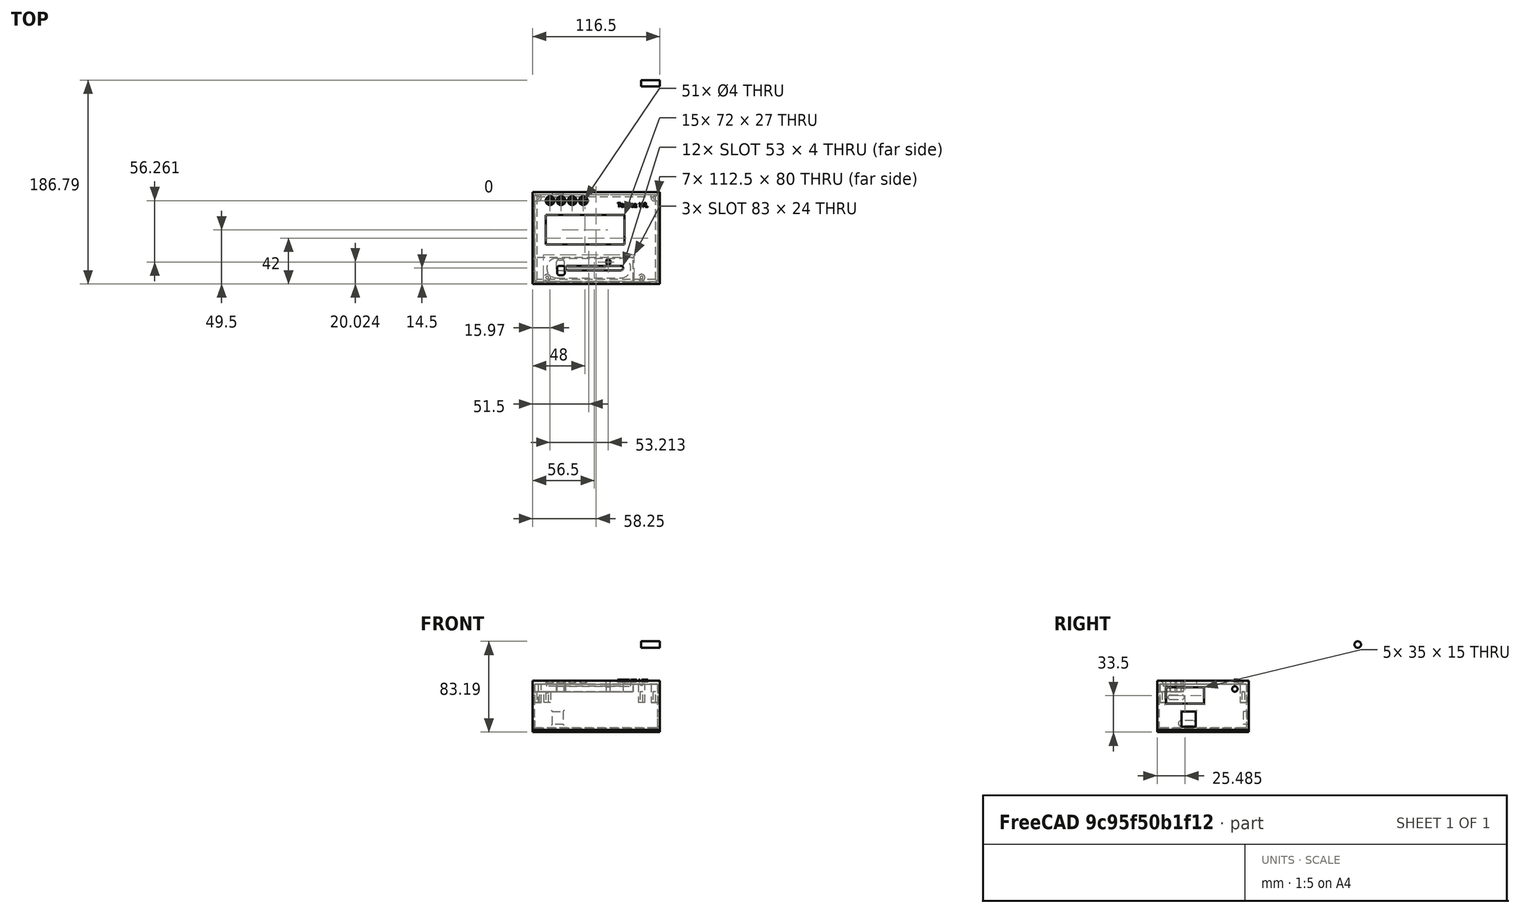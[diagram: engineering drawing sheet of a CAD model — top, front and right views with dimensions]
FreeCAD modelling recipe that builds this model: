
FCSTD DOCUMENT  (FreeCAD 0.17R7682 (Git))
Label: Modelodelgabinete4
License: CC-BY 3.0
LicenseURL: http://creativecommons.org/licenses/by/3.0/
objects: Sketcher::SketchObject×23, PartDesign::Pocket×14, PartDesign::Fillet×14, Part::Fillet×10, PartDesign::Pad×9, Part::Cut×6, Part::Extrusion×6, Drawing::FeatureViewPart×3, PartDesign::Chamfer×2, Part::Part2DObjectPython×1, Drawing::FeaturePage×1
note: 108 computed .brp shape members not serialized (recipe doc carries the construction recipe); baked Part::Feature solids carry a one-line shape summary decoded from their .brp

FEATURE [Sketcher::SketchObject] Sketch
  MapMode = 5
  sketch-geometry (5):
    g0: LineSegment StartX=0 StartY=0 StartZ=0 EndX=116.5 EndY=0 EndZ=0
    g1: LineSegment StartX=116.5 StartY=0 StartZ=0 EndX=116.5 EndY=-84 EndZ=0
    g2: LineSegment StartX=116.5 StartY=-84 StartZ=0 EndX=0 EndY=-84 EndZ=0
    g3: LineSegment StartX=0 StartY=-84 StartZ=0 EndX=0 EndY=0 EndZ=0
    g4: GeomPoint [constr] X=0 Y=0 Z=0
  constraints (12):
    c: Coincident(g0,g1)
    c: Coincident(g1,g2)
    c: Coincident(g2,g3)
    c: Coincident(g3,g0)
    c: Horizontal(g0)
    c: Horizontal(g2)
    c: Vertical(g1)
    c: Vertical(g3)
    c: Coincident(g4,g-1)
    c: Coincident(g0,g-1)
    c: DistanceX(g0) = 116.5
    c: DistanceY(g3) = 84
FEATURE [PartDesign::Pad] Pad
  Length = 45
  Length2 = 100
  Type = 0
FEATURE [Sketcher::SketchObject] Sketch001
  MapMode = 5
  Placement = pos=(0,0,0) rot=(1,0,0;1.5708rad)
  sketch-geometry (4):
    g0: LineSegment StartX=18 StartY=5 StartZ=0 EndX=28 EndY=5 EndZ=0
    g1: LineSegment StartX=28 StartY=5 StartZ=0 EndX=28 EndY=17 EndZ=0
    g2: LineSegment StartX=28 StartY=17 StartZ=0 EndX=18 EndY=17 EndZ=0
    g3: LineSegment StartX=18 StartY=17 StartZ=0 EndX=18 EndY=5 EndZ=0
  constraints (12):
    c: Coincident(g0,g1)
    c: Coincident(g1,g2)
    c: Coincident(g2,g3)
    c: Coincident(g3,g0)
    c: Horizontal(g0)
    c: Horizontal(g2)
    c: Vertical(g1)
    c: Vertical(g3)
    c: DistanceX(g-1,g0) = 18
    c: DistanceY(g-1,g0) = 5
    c: DistanceX(g0) = 10
    c: DistanceY(g1) = 12
FEATURE [PartDesign::Pad] Pad001
  Length = 5
  Length2 = 100
  Placement = pos=(0,0,0) rot=(1,0,0;1.5708rad)
  Type = 0
FEATURE [Part::Cut] Cut
  Base = -> Pad
  Tool = -> Pad001
FEATURE [Sketcher::SketchObject] Sketch002
  MapMode = 5
  Placement = pos=(0,0,45) rot=(0,0,1;0rad)
  sketch-geometry (4):
    g0: LineSegment StartX=11.5 StartY=-20.5 StartZ=0 EndX=84.5 EndY=-20.5 EndZ=0
    g1: LineSegment StartX=84.5 StartY=-20.5 StartZ=0 EndX=84.5 EndY=-48.5 EndZ=0
    g2: LineSegment StartX=84.5 StartY=-48.5 StartZ=0 EndX=11.5 EndY=-48.5 EndZ=0
    g3: LineSegment StartX=11.5 StartY=-48.5 StartZ=0 EndX=11.5 EndY=-20.5 EndZ=0
  constraints (12):
    c: Coincident(g0,g1)
    c: Coincident(g1,g2)
    c: Coincident(g2,g3)
    c: Coincident(g3,g0)
    c: Horizontal(g0)
    c: Horizontal(g2)
    c: Vertical(g1)
    c: Vertical(g3)
    c: DistanceY(g-1,g0) = -20.5
    c: DistanceX(g-1,g0) = 11.5
    c: DistanceY(g3) = 28
    c: DistanceX(g2) = -73
FEATURE [PartDesign::Pocket] Pocket
  Length = 5
  Type = 0
FEATURE [Sketcher::SketchObject] Sketch003
  MapMode = 5
  sketch-geometry (4):
    g0: LineSegment StartX=2 StartY=-2 StartZ=0 EndX=114.5 EndY=-2 EndZ=0
    g1: LineSegment StartX=114.5 StartY=-2 StartZ=0 EndX=114.5 EndY=-82 EndZ=0
    g2: LineSegment StartX=114.5 StartY=-82 StartZ=0 EndX=2 EndY=-82 EndZ=0
    g3: LineSegment StartX=2 StartY=-82 StartZ=0 EndX=2 EndY=-2 EndZ=0
  constraints (12):
    c: Coincident(g0,g1)
    c: Coincident(g1,g2)
    c: Coincident(g2,g3)
    c: Coincident(g3,g0)
    c: Horizontal(g0)
    c: Horizontal(g2)
    c: Vertical(g1)
    c: Vertical(g3)
    c: DistanceY(g-1,g0) = -2
    c: DistanceX(g-1,g0) = 2
    c: DistanceX(g2) = -112.5
    c: DistanceY(g1) = -80
FEATURE [PartDesign::Pad] Pad002
  Length = 42
  Length2 = 100
  Type = 0
FEATURE [Part::Cut] Cut001
  Base = -> Pocket
  Tool = -> Pad002
FEATURE [Sketcher::SketchObject] Sketch004
  ExternalGeometry = -> [Cut001]
  MapMode = 5
  Placement = pos=(0,0,0) rot=(0.57735,-0.57735,-0.57735;2.0944rad)
  sketch-geometry (4):
    g0: ArcOfCircle CenterX=72 CenterY=30 CenterZ=0 NormalX=0 NormalY=0 NormalZ=1 Radius=2 StartAngle=4.7124 EndAngle=7.85397
    g1: ArcOfCircle CenterX=61 CenterY=30 CenterZ=0 NormalX=0 NormalY=0 NormalZ=1 Radius=2 StartAngle=1.57079 EndAngle=4.71239
    g2: LineSegment StartX=72 StartY=32 StartZ=0 EndX=61 EndY=32 EndZ=0
    g3: LineSegment StartX=72 StartY=28 StartZ=0 EndX=61 EndY=28 EndZ=0
  constraints (14):
    c: Tangent(g0,g2)
    c: Tangent(g0,g3)
    c: Tangent(g1,g2)
    c: Tangent(g1,g3)
    c: Coincident(g0,g3)
    c: Coincident(g0,g2)
    c: Coincident(g2,g1)
    c: Coincident(g3,g1)
    c: Horizontal(g2)
    c: Equal(g0,g1)
    c: DistanceX(g0,g-3) = 12
    c: DistanceX(g1,g0) = 11
    c: Radius(g0) = 2
    c: DistanceY(g-3,g0) = 30
FEATURE [PartDesign::Pocket] Pocket001
  Length = 5
  Type = 0
FEATURE [Sketcher::SketchObject] Sketch005
  MapMode = 5
  Placement = pos=(0,0,0) rot=(0.57735,-0.57735,-0.57735;2.0944rad)
  sketch-geometry (4):
    g0: ArcOfCircle CenterX=51 CenterY=6 CenterZ=0 NormalX=0 NormalY=0 NormalZ=1 Radius=2.5 StartAngle=1.57079 EndAngle=4.71239
    g1: ArcOfCircle CenterX=62 CenterY=6 CenterZ=0 NormalX=0 NormalY=0 NormalZ=1 Radius=2.5 StartAngle=4.7124 EndAngle=7.85397
    g2: LineSegment StartX=51 StartY=3.5 StartZ=0 EndX=62 EndY=3.5 EndZ=0
    g3: LineSegment StartX=51 StartY=8.5 StartZ=0 EndX=62 EndY=8.5 EndZ=0
  constraints (13):
    c: Tangent(g0,g2)
    c: Tangent(g0,g3)
    c: Tangent(g1,g2)
    c: Tangent(g1,g3)
    c: Coincident(g0,g3)
    c: Coincident(g0,g2)
    c: Coincident(g2,g1)
    c: Coincident(g3,g1)
    c: Horizontal(g2)
    c: Equal(g0,g1)
    c: DistanceY(g-1,g0) = 6
    c: Radius(g0) = 2.5
    c: DistanceX(g0,g1) = 11
FEATURE [PartDesign::Pocket] Pocket002
  Length = 5
  Type = 0
FEATURE [Sketcher::SketchObject] Sketch006
  ExternalGeometry = -> [Pocket002]
  MapMode = 5
  Placement = pos=(0,0,45) rot=(0,0,1;0rad)
  sketch-geometry (4):
    g0: ArcOfCircle CenterX=32 CenterY=-69.5 CenterZ=0 NormalX=0 NormalY=0 NormalZ=1 Radius=2 StartAngle=1.5708 EndAngle=4.71239
    g1: ArcOfCircle CenterX=81 CenterY=-69.5 CenterZ=0 NormalX=0 NormalY=0 NormalZ=1 Radius=2 StartAngle=4.71239 EndAngle=7.85398
    g2: LineSegment StartX=32 StartY=-71.5 StartZ=0 EndX=81 EndY=-71.5 EndZ=0
    g3: LineSegment StartX=32 StartY=-67.5 StartZ=0 EndX=81 EndY=-67.5 EndZ=0
  constraints (14):
    c: Tangent(g0,g2)
    c: Tangent(g0,g3)
    c: Tangent(g1,g2)
    c: Tangent(g1,g3)
    c: Coincident(g0,g3)
    c: Coincident(g0,g2)
    c: Coincident(g2,g1)
    c: Coincident(g3,g1)
    c: Horizontal(g2)
    c: Equal(g0,g1)
    c: DistanceY(g-3,g0) = 14.5
    c: Radius(g1) = 2
    c: DistanceX(g0,g-3) = -32
    c: DistanceX(g0,g1) = 49
FEATURE [PartDesign::Pocket] Pocket003
  Length = 5
  Type = 0
FEATURE [PartDesign::Pocket] Pocket004
  Length = 5
  Type = 0
FEATURE [Sketcher::SketchObject] Sketch008
  MapMode = 5
  Placement = pos=(0,0,45) rot=(0,0,1;0rad)
  sketch-geometry (5):
    g0: Circle CenterX=15.97 CenterY=-7.715 CenterZ=0 NormalX=0 NormalY=0 NormalZ=1 Radius=2
    g1: Circle CenterX=26.13 CenterY=-7.715 CenterZ=0 NormalX=0 NormalY=0 NormalZ=1 Radius=2
    g2: Circle CenterX=36.29 CenterY=-7.715 CenterZ=0 NormalX=0 NormalY=0 NormalZ=1 Radius=2
    g3: Circle CenterX=46.45 CenterY=-7.715 CenterZ=0 NormalX=0 NormalY=0 NormalZ=1 Radius=2
    g4: Circle CenterX=69.183 CenterY=-63.976 CenterZ=0 NormalX=0 NormalY=0 NormalZ=1 Radius=2
  constraints (15):
    c: DistanceX(g-1,g0) = 15.97
    c: Radius(g0) = 2
    c: Equal(g1,g0)
    c: DistanceY(g1,g0) = 0
    c: DistanceX(g1,g0) = -10.16
    c: Equal(g1,g2)
    c: DistanceX(g2,g1) = -10.16
    c: DistanceY(g1,g2) = 0
    c: Equal(g3,g2)
    c: DistanceY(g2,g3) = 0
    c: DistanceX(g2,g3) = 10.16
    c: DistanceY(g-1,g0) = -7.715
    c: DistanceX(g-1,g4) = 69.183
    c: Radius(g4) = 2
    c: DistanceY(g-1,g4) = -63.976
FEATURE [PartDesign::Pocket] Pocket005
  Length = 10
  Type = 2
FEATURE [Sketcher::SketchObject] Sketch009
  MapMode = 5
  Placement = pos=(116.5,0,0) rot=(0.57735,0.57735,0.57735;2.0944rad)
  sketch-geometry (12):
    g0: LineSegment StartX=-76.015 StartY=39 StartZ=0 EndX=-41.015 EndY=39 EndZ=0
    g1: LineSegment StartX=-41.015 StartY=39 StartZ=0 EndX=-41.015 EndY=24 EndZ=0
    g2: LineSegment StartX=-41.015 StartY=24 StartZ=0 EndX=-76.015 EndY=24 EndZ=0
    g3: LineSegment StartX=-76.015 StartY=24 StartZ=0 EndX=-76.015 EndY=39 EndZ=0
    g4: LineSegment [constr] StartX=-58.515 StartY=5.11299 StartZ=0 EndX=-58.515 EndY=39.8089 EndZ=0
    g5: LineSegment [constr] StartX=-79.1576 StartY=31.5 StartZ=0 EndX=-35.4167 EndY=31.5 EndZ=0
    g6: LineSegment [constr] StartX=-61.5 StartY=10 StartZ=0 EndX=-48.5 EndY=10 EndZ=0
    g7: LineSegment StartX=-61.5 StartY=17 StartZ=0 EndX=-48.5 EndY=17 EndZ=0
    g8: LineSegment StartX=-48.5 StartY=17 StartZ=0 EndX=-48.5 EndY=3 EndZ=0
    g9: LineSegment StartX=-48.5 StartY=3 StartZ=0 EndX=-61.5 EndY=3 EndZ=0
    g10: LineSegment StartX=-61.5 StartY=3 StartZ=0 EndX=-61.5 EndY=17 EndZ=0
    g11: LineSegment [constr] StartX=-55 StartY=3 StartZ=0 EndX=-55 EndY=17 EndZ=0
  constraints (39):
    c: Coincident(g0,g1)
    c: Coincident(g1,g2)
    c: Coincident(g2,g3)
    c: Coincident(g3,g0)
    c: Horizontal(g0)
    c: Horizontal(g2)
    c: Vertical(g1)
    c: Vertical(g3)
    c: Vertical(g4)
    c: DistanceX(g-1,g4) = -58.515
    c: Symmetric(g2,g1,g4)
    c: Horizontal(g5)
    c: DistanceY(g-1,g5) = 31.5
    c: Symmetric(g0,g2,g5)
    c: DistanceY(g3) = 15
    c: DistanceX(g0,g0) = -35
    c: DistanceY(g4) = 34.6959
    c: DistanceX(g5) = 43.7409
    c: DistanceY(g-1,g4) = 5.11299
    c: DistanceX(g-1,g5) = -35.4167
    c: Horizontal(g6)
    c: DistanceY(g-1,g6) = 10
    c: Coincident(g7,g8)
    c: Coincident(g8,g9)
    c: Coincident(g9,g10)
    c: Coincident(g10,g7)
    c: Horizontal(g7)
    c: Horizontal(g9)
    c: Vertical(g8)
    c: Vertical(g10)
    c: Symmetric(g7,g8,g6)
    c: Vertical(g11)
    c: Symmetric(g7,g7,g11)
    c: DistanceX(g7) = 13
    c: DistanceY(g8) = -14
    c: PointOnObject(g11,g9)
    c: PointOnObject(g11,g7)
    c: PointOnObject(g6,g10)
    c: PointOnObject(g6,g8)
FEATURE [PartDesign::Pocket] Pocket006
  Length = 5
  Type = 0
FEATURE [Sketcher::SketchObject] Sketch010
  MapMode = 5
  Placement = pos=(0,0,42) rot=(1,0,0;3.14159rad)
  sketch-geometry (4):
    g0: LineSegment StartX=92 StartY=60 StartZ=0 EndX=2 EndY=60 EndZ=0
    g1: LineSegment StartX=2 StartY=60 StartZ=0 EndX=2 EndY=82 EndZ=0
    g2: LineSegment StartX=2 StartY=82 StartZ=0 EndX=92 EndY=82 EndZ=0
    g3: LineSegment StartX=92 StartY=82 StartZ=0 EndX=92 EndY=60 EndZ=0
  constraints (12):
    c: Coincident(g0,g1)
    c: Coincident(g1,g2)
    c: Coincident(g2,g3)
    c: Coincident(g3,g0)
    c: Horizontal(g0)
    c: Horizontal(g2)
    c: Vertical(g1)
    c: Vertical(g3)
    c: DistanceX(g-1,g0) = 2
    c: DistanceY(g-1,g1) = 82
    c: DistanceX(g0) = -90
    c: DistanceY(g3) = -22
FEATURE [PartDesign::Pad] Pad003
  Length = 7
  Length2 = 100
  Type = 0
FEATURE [Part::Extrusion] Extrude001
  Base = -> Sketch006
  Dir = (0,0,15)
  Placement = pos=(0,0,-15) rot=(0,0,1;0rad)
  Solid = true
FEATURE [Part::Extrusion] Extrude002
  Base = -> Sketch008
  Dir = (0,0,15)
  Placement = pos=(0,0,-15) rot=(0,0,1;0rad)
  Solid = true
FEATURE [PartDesign::Pocket] Pocket007
  Length = 5
  Type = 0
FEATURE [PartDesign::Fillet] Fillet
  Base = -> Pocket007 [Edge142]
  Radius = 1
FEATURE [PartDesign::Fillet] Fillet001
  Base = -> Fillet [Edge20]
  Radius = 1
FEATURE [PartDesign::Fillet] Fillet002
  Base = -> Fillet001 [Edge140]
  Radius = 1
FEATURE [PartDesign::Chamfer] Chamfer
  Base = -> Fillet002 [Edge141]
  Size = 1
FEATURE [PartDesign::Chamfer] Chamfer001
  Base = -> Chamfer [Edge76,Edge77,Edge75,Edge74]
  Size = 1
FEATURE [PartDesign::Fillet] Fillet003
  Base = -> Chamfer001 [Edge43,Edge40,Edge41,Edge42,Edge38,Edge39,Edge37,Edge36]
  Radius = 1
FEATURE [PartDesign::Fillet] Fillet004
  Base = -> Fillet003 [Edge48,Edge47,Edge46,Edge45]
  Radius = 1
FEATURE [PartDesign::Fillet] Fillet005
  Base = -> Fillet004 [Edge52,Edge50,Edge49,Edge51,Edge53,Edge56,Edge54,Edge55]
  Radius = 1
FEATURE [Sketcher::SketchObject] Sketch012
  ExternalGeometry = -> [Fillet005]
  MapMode = 5
  Placement = pos=(0,0,35) rot=(1,0,0;3.14159rad)
  sketch-geometry (1):
    g0: Circle CenterX=13.43 CenterY=78.19 CenterZ=0 NormalX=0 NormalY=0 NormalZ=1 Radius=3
  constraints (3):
    c: DistanceY(g0,g-3) = 5.81
    c: DistanceX(g0,g-3) = -13.43
    c: Radius(g0) = 3
FEATURE [PartDesign::Pad] Pad004
  Length = 10
  Length2 = 100
  Type = 0
FEATURE [Sketcher::SketchObject] Sketch013
  ExternalGeometry = -> [Pad004]
  MapMode = 5
  Placement = pos=(116.5,0,0) rot=(0.57735,0.57735,0.57735;2.0944rad)
  sketch-geometry (1):
    g0: Circle CenterX=99.79 CenterY=78.19 CenterZ=0 NormalX=0 NormalY=0 NormalZ=1 Radius=3
  constraints (3):
    c: DistanceY(g-3,g0) = 0
    c: DistanceX(g-3,g0) = 86.36
    c: Radius(g0) = 3
FEATURE [PartDesign::Pad] Pad005
  Length = 17
  Length2 = 100
  Reversed = true
  Type = 0
FEATURE [Sketcher::SketchObject] Sketch015
  MapMode = 5
  Placement = pos=(0,0,42) rot=(1,0,0;3.14159rad)
  sketch-geometry (7):
    g0: LineSegment StartX=108.5 StartY=2 StartZ=0 EndX=114.5 EndY=2 EndZ=0
    g1: LineSegment StartX=114.5 StartY=2 StartZ=0 EndX=114.5 EndY=8 EndZ=0
    g2: LineSegment StartX=114.5 StartY=8 StartZ=0 EndX=111.5 EndY=8 EndZ=0
    g3: LineSegment StartX=108.5 StartY=5 StartZ=0 EndX=108.5 EndY=2 EndZ=0
    g4: ArcOfCircle CenterX=111.5 CenterY=5 CenterZ=0 NormalX=0 NormalY=0 NormalZ=1 Radius=3 StartAngle=1.5708 EndAngle=3.14159
    g5: GeomPoint [constr] X=111.922 Y=0 Z=0
    g6: GeomPoint [constr] X=114.5 Y=3.11972 Z=0
  constraints (17):
    c: Coincident(g0,g1)
    c: Coincident(g1,g2)
    c: Coincident(g3,g0)
    c: Horizontal(g0)
    c: Horizontal(g2)
    c: Vertical(g1)
    c: Vertical(g3)
    c: Radius(g4) = 3
    c: DistanceY(g1) = 6
    c: PointOnObject(g5,g-1)
    c: DistanceY(g5,g0) = 2
    c: DistanceX(g0,g6) = 0
    c: PointOnObject(g4,g4)
    c: DistanceX(g4,g0) = 3
    c: DistanceX(g0) = 6
    c: Coincident(g4,g2)
    c: Coincident(g4,g3)
FEATURE [PartDesign::Pad] Pad007
  Length = 17
  Length2 = 100
  Placement = pos=(0,0,42) rot=(1,0,0;3.14159rad)
  Type = 0
FEATURE [Sketcher::SketchObject] Sketch016
  MapMode = 5
  Placement = pos=(0,0,25) rot=(1,0,0;3.14159rad)
  sketch-geometry (1):
    g0: Circle CenterX=111.5 CenterY=5 CenterZ=0 NormalX=0 NormalY=0 NormalZ=1 Radius=1.25
FEATURE [PartDesign::Pocket] Pocket008
  Length = 10
  Type = 0
FEATURE [Sketcher::SketchObject] Sketch017
  ExternalGeometry = -> [Pocket008]
  MapMode = 5
  Placement = pos=(0,0,25) rot=(1,0,0;3.14159rad)
  sketch-geometry (1):
    g0: Circle CenterX=5 CenterY=5 CenterZ=0 NormalX=0 NormalY=0 NormalZ=1 Radius=1.25
  constraints (2):
    c: Coincident(g-3,g0)
    c: Radius(g0) = 1.25
FEATURE [PartDesign::Pocket] Pocket009
  Length = 10
  Type = 0
FEATURE [Sketcher::SketchObject] Sketch018
  ExternalGeometry = -> [Pocket009]
  MapMode = 5
  Placement = pos=(0,0,25) rot=(1,0,0;3.14159rad)
  sketch-geometry (1):
    g0: Circle CenterX=13.43 CenterY=78.19 CenterZ=0 NormalX=0 NormalY=0 NormalZ=1 Radius=1.25
  constraints (2):
    c: Coincident(g0,g-3)
    c: Radius(g0) = 1.25
FEATURE [PartDesign::Pocket] Pocket010
  Length = 10
  Type = 0
FEATURE [Sketcher::SketchObject] Sketch019
  ExternalGeometry = -> [Pocket010]
  MapMode = 5
  Placement = pos=(0,0,25) rot=(1,0,0;3.14159rad)
  sketch-geometry (1):
    g0: Circle CenterX=99.79 CenterY=78.19 CenterZ=0 NormalX=0 NormalY=0 NormalZ=1 Radius=1.25
  constraints (2):
    c: Coincident(g0,g-3)
    c: Radius(g0) = 1.25
FEATURE [PartDesign::Pocket] Pocket011
  Length = 10
  Type = 0
FEATURE [PartDesign::Fillet] Fillet006
  Base = -> Pocket011 [Edge180,Edge165,Edge174,Edge158]
  Radius = 1
FEATURE [PartDesign::Fillet] Fillet007
  Base = -> Fillet006 [Edge9,Edge30,Edge4,Edge1]
  Radius = 1
FEATURE [PartDesign::Fillet] Fillet008
  Base = -> Fillet007 [Edge84]
  Radius = 1
FEATURE [PartDesign::Fillet] Fillet009
  Base = -> Fillet008 [Edge18]
  Radius = 1
FEATURE [PartDesign::Fillet] Fillet010
  Base = -> Fillet009 [Edge28]
  Radius = 1
FEATURE [PartDesign::Fillet] Fillet011
  Base = -> Fillet010 [Edge36]
  Radius = 1
FEATURE [Part::Part2DObjectPython] ShapeString  # Draft 2D object (typed FeaturePython)
  FontFile = <path>
  Placement = pos=(77.6058,-13.5175,45) rot=(0,0,1;0rad)
  Size = 2
  String = Tecnica 1VL
  Tracking = 0
FEATURE [Part::Extrusion] Extrude003
  Base = -> ShapeString
  Dir = (0,0,1)
  Solid = true
FEATURE [Part::Extrusion] Extrude004
  Base = -> ShapeString
  Dir = (0,0,1)
  Solid = true
FEATURE [Part::Extrusion] Extrude005
  Base = -> ShapeString
  Dir = (0,0,1)
  Placement = pos=(0,0,-1) rot=(0,0,1;0rad)
  Solid = true
FEATURE [Part::Cut] Cut005
  Base = -> Fillet011
  Tool = -> Extrude005
FEATURE [PartDesign::Fillet] Fillet012
  Base = -> Cut005 [Edge162,Edge161]
  Radius = 1
FEATURE [PartDesign::Fillet] Fillet013
  Base = -> Fillet012 [Edge22]
  Radius = 1
FEATURE [Sketcher::SketchObject] Sketch007
  ExternalGeometry = -> [Fillet013]
  MapMode = 5
  Placement = pos=(0,0,45) rot=(0,0,1;0rad)
  sketch-geometry (9):
    g0: LineSegment StartX=24.5 StartY=-67.5 StartZ=0 EndX=27.5 EndY=-67.5 EndZ=0
    g1: LineSegment StartX=29.5 StartY=-69.5 StartZ=0 EndX=29.5 EndY=-74 EndZ=0
    g2: LineSegment StartX=27.5 StartY=-76 StartZ=0 EndX=24.5 EndY=-76 EndZ=0
    g3: LineSegment StartX=22.5 StartY=-74 StartZ=0 EndX=22.5 EndY=-69.5 EndZ=0
    g4: ArcOfCircle CenterX=24.5 CenterY=-74 CenterZ=0 NormalX=0 NormalY=0 NormalZ=1 Radius=2 StartAngle=3.14159 EndAngle=4.71239
    g5: ArcOfCircle CenterX=24.5 CenterY=-69.5 CenterZ=0 NormalX=0 NormalY=0 NormalZ=1 Radius=2 StartAngle=1.5708 EndAngle=3.14159
    g6: ArcOfCircle CenterX=27.5 CenterY=-69.5 CenterZ=0 NormalX=0 NormalY=0 NormalZ=1 Radius=2 StartAngle=0 EndAngle=1.5708
    g7: ArcOfCircle CenterX=27.5 CenterY=-74 CenterZ=0 NormalX=0 NormalY=0 NormalZ=1 Radius=2 StartAngle=4.71239 EndAngle=6.28319
    g8: LineSegment [constr] StartX=32 StartY=-69.5 StartZ=0 EndX=18.3618 EndY=-69.5 EndZ=0
  constraints (24):
    c: Horizontal(g0)
    c: Horizontal(g2)
    c: Vertical(g1)
    c: Vertical(g3)
    c: Tangent(g3,g4)
    c: Tangent(g2,g4)
    c: Tangent(g3,g5)
    c: Tangent(g0,g5)
    c: Tangent(g0,g6)
    c: Tangent(g1,g6)
    c: Tangent(g2,g7)
    c: Tangent(g1,g7)
    c: Coincident(g8,g-3)
    c: Horizontal(g8)
    c: DistanceX(g8,g8) = 13.6382
    c: DistanceY(g7,g6) = 4.5
    c: DistanceX(g5,g6) = 3
    c: Radius(g6) = 2
    c: Radius(g7) = 2
    c: Radius(g4) = 2
    c: Radius(g5) = 2
    c: PointOnObject(g6,g8)
    c: DistanceX(g6,g8) = 4.5
    c: Radius(g-3) = 2
FEATURE [Part::Extrusion] Extrude
  Base = -> Sketch007
  Dir = (0,0,13)
  Placement = pos=(0,0,-13) rot=(0,0,1;0rad)
  Solid = true
FEATURE [Part::Cut] Cut002
  Base = -> Pad003
  Tool = -> Extrude
FEATURE [Part::Cut] Cut003
  Base = -> Cut002
  Tool = -> Extrude001
FEATURE [Part::Cut] Cut004
  Base = -> Cut003
  Tool = -> Extrude002
FEATURE [Sketcher::SketchObject] Sketch011
  ExternalGeometry = -> [Cut004]
  MapMode = 5
  Placement = pos=(0,0,45) rot=(0,0,1;0rad)
  sketch-geometry (4):
    g0: ArcOfCircle CenterX=22.5 CenterY=-69.5 CenterZ=0 NormalX=0 NormalY=0 NormalZ=1 Radius=9 StartAngle=1.5708 EndAngle=4.71239
    g1: ArcOfCircle CenterX=81 CenterY=-69.5 CenterZ=0 NormalX=0 NormalY=0 NormalZ=1 Radius=9 StartAngle=4.71239 EndAngle=7.85398
    g2: LineSegment StartX=22.5 StartY=-78.5 StartZ=0 EndX=81 EndY=-78.5 EndZ=0
    g3: LineSegment StartX=22.5 StartY=-60.5 StartZ=0 EndX=81 EndY=-60.5 EndZ=0
  constraints (14):
    c: Tangent(g0,g2)
    c: Tangent(g0,g3)
    c: Tangent(g1,g2)
    c: Tangent(g1,g3)
    c: Coincident(g0,g3)
    c: Coincident(g0,g2)
    c: Coincident(g2,g1)
    c: Coincident(g3,g1)
    c: Horizontal(g2)
    c: Equal(g0,g1)
    c: DistanceY(g1,g-3) = 0
    c: Coincident(g1,g-3)
    c: PointOnObject(g0,g-4)
    c: Distance(g1,g1) = 18
FEATURE [Drawing::FeatureViewPart] Ortho  label="Ortho_0_0"
  Direction = (1,0,0)
  HiddenWidth = 0.15
  LineWidth = 0.35
  Rotation = -90
  ShowHiddenLines = false
  ShowSmoothLines = false
  Source = -> Fillet013
  Tolerance = 0.05
  ViewResult = <blob: 6998 chars omitted>
  Visible = true
  X = 120.5
  Y = 72.3333
FEATURE [Drawing::FeatureViewPart] Ortho001  label="Ortho_0_-1"
  Direction = (0,0,-1)
  HiddenWidth = 0.15
  LineWidth = 0.35
  Rotation = 90
  ShowHiddenLines = false
  ShowSmoothLines = false
  Source = -> Fillet013
  Tolerance = 0.05
  ViewResult = <blob: 3870 chars omitted>
  Visible = true
  X = 120.5
  Y = 191.604
FEATURE [Drawing::FeatureViewPart] Ortho002  label="Ortho_1_0"
  Direction = (0,1,0)
  HiddenWidth = 0.15
  LineWidth = 0.35
  Rotation = -90
  ShowHiddenLines = false
  ShowSmoothLines = false
  Source = -> Fillet013
  Tolerance = 0.05
  ViewResult = <blob: 12460 chars omitted>
  Visible = true
  X = 248.938
  Y = 72.3333
FEATURE [Drawing::FeaturePage] Page
  EditableTexts = Designed by Name | Date | Scale | Weight | Title | Subtitle | Drawing number | Sheet
  Group = -> [Ortho,Ortho001,Ortho002]
  Template = <path>
FEATURE [Sketcher::SketchObject] Sketch020
  ExternalGeometry = -> [Fillet013]
  MapMode = 5
  Placement = pos=(116.5,0,0) rot=(0.57735,0.57735,0.57735;2.0944rad)
  Support = -> [Fillet013]
  sketch-geometry (2):
    g0: Circle CenterX=-12.8 CenterY=37.5 CenterZ=0 NormalX=0 NormalY=0 NormalZ=1 Radius=2.5
    g1: LineSegment [constr] StartX=-40.015 StartY=40 StartZ=0 EndX=-0.8 EndY=40 EndZ=0
  constraints (6):
    c: Radius(g0) = 2.5
    c: Coincident(g1,g-4)
    c: PointOnObject(g1,g-3)
    c: Horizontal(g1)
    c: Tangent(g0,g1)
    c: DistanceX(g0,g-3) = 12
FEATURE [PartDesign::Pocket] Pocket012
  Length = 5
  Profile = -> Sketch020
  Type = 2
FEATURE [Sketcher::SketchObject] Sketch021
  ExternalGeometry = -> [Pocket012]
  Placement = pos=(0,0,0) rot=(-1,0,0;3.14159rad)
  sketch-geometry (4):
    g0: LineSegment StartX=0 StartY=0 StartZ=0 EndX=116.5 EndY=0 EndZ=0
    g1: LineSegment StartX=116.5 StartY=0 StartZ=0 EndX=116.5 EndY=84 EndZ=0
    g2: LineSegment StartX=116.5 StartY=84 StartZ=0 EndX=0 EndY=84 EndZ=0
    g3: LineSegment StartX=0 StartY=84 StartZ=0 EndX=0 EndY=0 EndZ=0
  constraints (11):
    c: Coincident(g0,g1)
    c: Coincident(g1,g2)
    c: Coincident(g2,g3)
    c: Coincident(g3,g0)
    c: Horizontal(g0)
    c: Horizontal(g2)
    c: Vertical(g1)
    c: Vertical(g3)
    c: Coincident(g0,g-1)
    c: PointOnObject(g-3,g2)
    c: PointOnObject(g-4,g1)
FEATURE [PartDesign::Pad] Pad008
  Length = 2
  Length2 = 100
  Placement = pos=(0,0,0) rot=(-1,0,0;3.14159rad)
  Profile = -> Sketch021
  Type = 0
FEATURE [Sketcher::SketchObject] Sketch022
  ExternalGeometry = -> [Pad008]
  MapMode = 5
  Support = -> [Pad008]
  sketch-geometry (4):
    g0: LineSegment StartX=114.5 StartY=-82 StartZ=0 EndX=2 EndY=-82 EndZ=0
    g1: LineSegment StartX=2 StartY=-82 StartZ=0 EndX=2 EndY=-2 EndZ=0
    g2: LineSegment StartX=2 StartY=-2 StartZ=0 EndX=114.5 EndY=-2 EndZ=0
    g3: LineSegment StartX=114.5 StartY=-2 StartZ=0 EndX=114.5 EndY=-82 EndZ=0
  constraints (12):
    c: Coincident(g0,g1)
    c: Coincident(g1,g2)
    c: Coincident(g2,g3)
    c: Coincident(g3,g0)
    c: Horizontal(g0)
    c: Horizontal(g2)
    c: Vertical(g1)
    c: Vertical(g3)
    c: DistanceX(g2,g-4) = 2
    c: DistanceY(g2,g-4) = 2
    c: DistanceX(g-5,g0) = 2
    c: DistanceY(g-5,g0) = 2
FEATURE [PartDesign::Pad] Pad009
  Length = 2
  Length2 = 100
  Placement = pos=(0,0,0) rot=(-1,0,0;3.14159rad)
  Profile = -> Sketch022
  Type = 0
FEATURE [Sketcher::SketchObject] Sketch023
  ExternalGeometry = -> [Pad009]
  MapMode = 5
  Placement = pos=(0,0,2) rot=(0,0,1;0rad)
  Support = -> [Pad009]
  sketch-geometry (4):
    g0: LineSegment StartX=4 StartY=-4 StartZ=0 EndX=112.5 EndY=-4 EndZ=0
    g1: LineSegment StartX=112.5 StartY=-4 StartZ=0 EndX=112.5 EndY=-80 EndZ=0
    g2: LineSegment StartX=112.5 StartY=-80 StartZ=0 EndX=4 EndY=-80 EndZ=0
    g3: LineSegment StartX=4 StartY=-80 StartZ=0 EndX=4 EndY=-4 EndZ=0
  constraints (12):
    c: Coincident(g0,g1)
    c: Coincident(g1,g2)
    c: Coincident(g2,g3)
    c: Coincident(g3,g0)
    c: Horizontal(g0)
    c: Horizontal(g2)
    c: Vertical(g1)
    c: Vertical(g3)
    c: DistanceX(g1,g-5) = 2
    c: DistanceY(g-5,g1) = 2
    c: DistanceX(g-6,g0) = 2
    c: DistanceY(g0,g-6) = 2
FEATURE [PartDesign::Pocket] Pocket013
  Length = 2
  Placement = pos=(0,0,0) rot=(-1,0,0;3.14159rad)
  Profile = -> Sketch023
  Type = 0
FEATURE [Part::Fillet] Fillet014
  Base = -> Pocket013
  Edges = 1 edges r=1: [Edge22]
FEATURE [Part::Fillet] Fillet015
  Base = -> Fillet014
  Edges = 2 edges r=1: [Edge17,Edge21]
FEATURE [Part::Fillet] Fillet016
  Base = -> Fillet015
  Edges = 1 edges r=1: [Edge31]
FEATURE [Part::Fillet] Fillet017
  Base = -> Fillet016
  Edges = 2 edges r=1: [Edge20,Edge34]
FEATURE [Part::Fillet] Fillet018
  Base = -> Fillet017
  Edges = 2 edges r=1: [Edge22,Edge36]
FEATURE [Part::Fillet] Fillet019
  Base = -> Fillet018
  Edges = 1 edges r=1: [Edge50]
FEATURE [Part::Fillet] Fillet020
  Base = -> Fillet019
  Edges = 1 edges r=1: [Edge2]
FEATURE [Part::Fillet] Fillet021
  Base = -> Fillet020
  Edges = 1 edges r=0.5: [Edge12]
FEATURE [Part::Fillet] Fillet022
  Base = -> Fillet021
  Edges = 1 edges r=1: [Edge10]
FEATURE [Part::Fillet] Fillet023
  Base = -> Fillet022
  Edges = 1 edges r=1: [Edge2]
note: 2 file-system paths scrubbed to <path> (originals preserved in the JSON sidecar)
